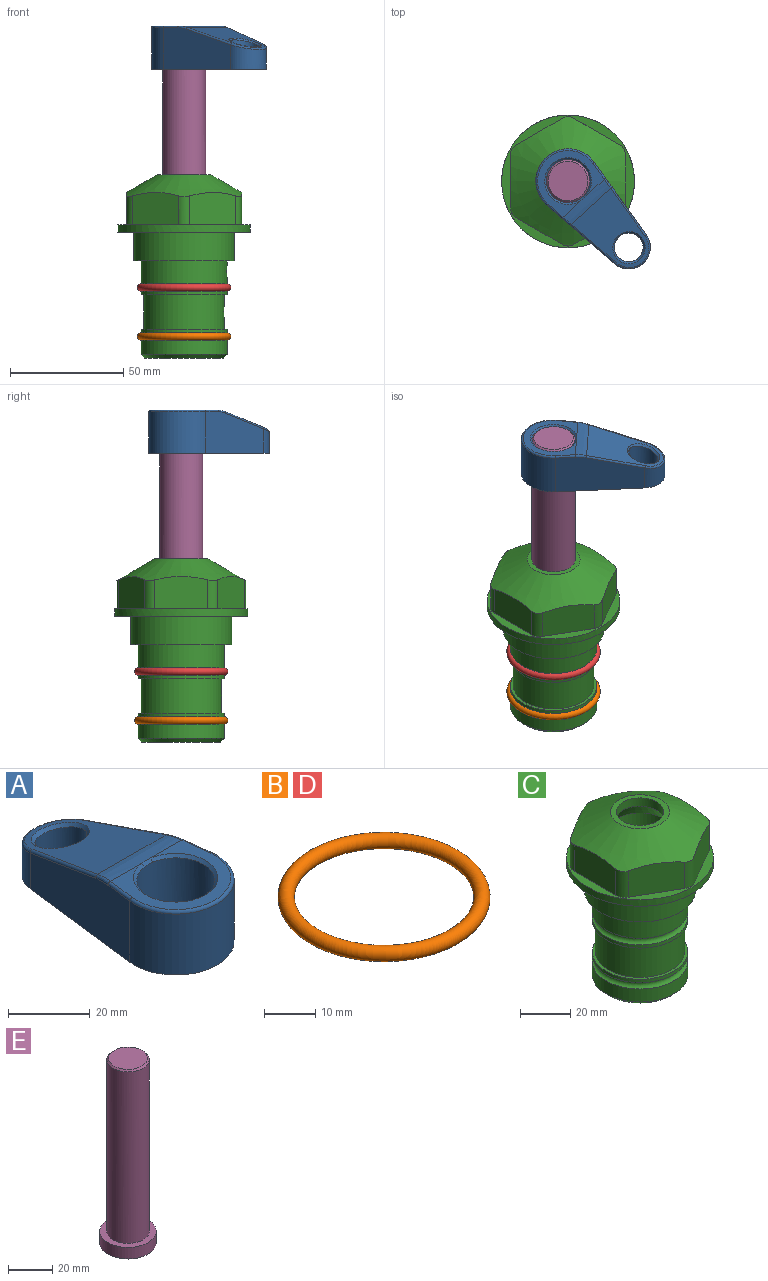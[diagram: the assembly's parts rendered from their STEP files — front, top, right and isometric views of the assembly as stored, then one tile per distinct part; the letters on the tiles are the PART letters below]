
ASSEMBLY  parts=5 mates=4
PART A: 31 faces, bbox 31.7x65.5x19.8 mm
  f0: plane 39.12x18.26mm, normal (0.99,0.12,0), area 612.2mm2, adj f1,f4,f7,f11,f13,f15
  f1: cylinder r=9.53mm len=18.91mm, axis (0,0,-1), area 296.1mm2, adj f0,f2,f7,f17
  f2: plane 39.12x18.26mm, normal (-0.99,0.12,0), area 612.2mm2, adj f1,f4,f7,f12,f14,f16
  f3: cylinder r=6.35mm len=12.7mm, axis (0,0,-1), area 362.4mm2, adj f7,f18
  f4: cylinder r=14.29mm len=28.58mm, axis (0,0,-1), area 882.2mm2, adj f0,f2,f7,f10
  f5: cylinder r=9.53mm len=19.05mm, axis (0,0,-1), area 1092.6mm2, adj f7,f19,f20
  f6: plane 26.99x23.69mm, normal (0,0,1), area 216.2mm2, adj f9,f10,f11,f12,f19
  f7: plane 63.5x28.58mm, normal (0,0,-1), area 661.8mm2, adj f0,f1,f2,f3,f4,f5,f22,f23
  f8: plane 33.52x23.6mm, normal (0,0.26,0.97), area 486mm2, adj f9,f15,f16,f17,f18
  f9: cylinder r=19.05mm len=24.72mm, axis (1,0,0), area 120.4mm2, adj f6,f8,f13,f14,f20
  f10: torus R=13.49mm, axis (0,0,1), area 59mm2, adj f4,f6,f11,f12
  f11: cylinder r=0.79mm len=8.67mm, axis (0.12,-0.99,0), area 10.8mm2, adj f0,f6,f10,f13
  f12: cylinder r=0.79mm len=8.67mm, axis (0.12,0.99,0), area 10.8mm2, adj f2,f6,f10,f14
  f13: bspline ~4.95x1.42mm, area 6.1mm2, adj f0,f9,f11,f15
  f14: bspline ~4.95x1.42mm, area 6.1mm2, adj f2,f9,f12,f16
  f15: cylinder r=0.79mm len=25.95mm, axis (0.12,-0.96,0.26), area 32.9mm2, adj f0,f8,f13,f17
  f16: cylinder r=0.79mm len=25.95mm, axis (0.12,0.96,-0.26), area 32.9mm2, adj f2,f8,f14,f17
  f17: bspline ~18.91x8.38mm, area 30mm2, adj f1,f8,f15,f16
  f18: bspline ~14.29x14.29mm, area 48.3mm2, adj f3,f8
  f19: cone r=9.53mm half-angle=45deg, axis (0,0,1), area 66.5mm2, adj f5,f6,f20
  f20: bspline ~3.22x0.96mm, area 3.5mm2, adj f5,f9,f19
  f21: plane 2.75x2.72mm, normal (0,0,-1), area 2.9mm2, adj f23,f25,f28
  f22: plane 23.05x15.88mm, normal (-0.99,-0.12,0), area 323.6mm2, adj f7,f25,f26,f27,f28,f29
  f23: plane 23.05x15.88mm, normal (0.99,-0.12,0), area 323.6mm2, adj f7,f21,f25,f27,f28,f30
  f24: cylinder r=9.53mm len=10.69mm, axis (0,0,-1), area 114.7mm2, adj f7,f27,f29,f30
  f25: cylinder r=12.7mm len=20.59mm, axis (0,0,-1), area 381.1mm2, adj f7,f21,f22,f23,f26,f28
  f26: plane 2.75x2.72mm, normal (0,0,-1), area 2.9mm2, adj f22,f25,f28
  f27: plane 19.72x18.37mm, normal (0,-0.26,-0.97), area 291.8mm2, adj f22,f23,f24,f28,f29,f30
  f28: cylinder r=15.88mm len=19.92mm, axis (1,0,0), area 54.8mm2, adj f21,f22,f23,f25,f26,f27
  f29: cylinder r=1.59mm len=11mm, axis (0,0,-1), area 34.7mm2, adj f7,f22,f24,f27
  f30: cylinder r=1.59mm len=11mm, axis (0,0,-1), area 34.7mm2, adj f7,f23,f24,f27
PART B: 1 faces, bbox 44.7x44.7x3.2 mm
  f0: torus R=19.05mm, axis (0,0,1), area 1193.9mm2
PART C: 36 faces, bbox 58.7x58.7x81 mm
  f0: cylinder r=17.78mm len=35.56mm, axis (0,0,1), area 1670.8mm2, adj f23,f24,f31
  f1: cylinder r=19.05mm len=38.1mm, axis (0,0,1), area 1191.9mm2, adj f26,f27,f30
  f2: plane 58.66x58.66mm, normal (0,0,-1), area 1150.6mm2, adj f3,f28
  f3: cylinder r=29.33mm len=58.66mm, axis (0,0,-1), area 585.1mm2, adj f2,f4
  f4: plane 58.66x58.66mm, normal (0,0,1), area 475.9mm2, adj f3,f5,f6,f7,f8,f9,f10,f11
  f5: plane 20.32x14.34mm, normal (-0.5,0.87,0), area 324.4mm2, adj f4,f15,f16,f17
  f6: plane 20.32x14.34mm, normal (0.5,0.87,0), area 324.4mm2, adj f4,f14,f15,f17
  f7: plane 23.48x14.34mm, normal (1,0,0), area 324.4mm2, adj f4,f13,f14,f17
  f8: plane 20.32x14.34mm, normal (0.5,-0.87,0), area 324.4mm2, adj f4,f12,f13,f17
  f9: plane 20.32x14.34mm, normal (-0.5,-0.87,0), area 324.4mm2, adj f4,f11,f12,f17
  f10: plane 23.48x14.34mm, normal (-1,0,0), area 324.4mm2, adj f4,f11,f16,f17
  f11: cylinder r=5.08mm len=12.85mm, axis (0,0,-1), area 67.2mm2, adj f4,f9,f10,f17
  f12: cylinder r=5.08mm len=12.85mm, axis (0,0,-1), area 67.2mm2, adj f4,f8,f9,f17
  f13: cylinder r=5.08mm len=12.85mm, axis (0,0,-1), area 67.2mm2, adj f4,f7,f8,f17
  f14: cylinder r=5.08mm len=12.85mm, axis (0,0,-1), area 67.2mm2, adj f4,f6,f7,f17
  f15: cylinder r=5.08mm len=12.85mm, axis (0,0,-1), area 67.2mm2, adj f4,f5,f6,f17
  f16: cylinder r=5.08mm len=12.85mm, axis (0,0,-1), area 67.2mm2, adj f4,f5,f10,f17
  f17: cone r=11.73mm half-angle=60deg, axis (0,0,-1), area 2071.8mm2, adj f5,f6,f7,f8,f9,f10,f11,f12
  f18: plane 23.46x23.46mm, normal (0,0,1), area 147.4mm2, adj f17,f35
  f19: plane 34.93x34.93mm, normal (0,0,-1), area 958mm2, adj f29
  f20: cylinder r=19.05mm len=38.1mm, axis (0,0,1), area 760.1mm2, adj f21,f29
  f21: torus R=19.05mm, axis (0,0,1), area 565.3mm2, adj f20,f22
  f22: cylinder r=19.05mm len=38.1mm, axis (0,0,1), area 190mm2, adj f21,f23
  f23: plane 38.1x38.1mm, normal (0,0,1), area 146.9mm2, adj f0,f22
  f24: plane 38.1x38.1mm, normal (0,0,-1), area 146.9mm2, adj f0,f25
  f25: cylinder r=19.05mm len=38.1mm, axis (0,0,1), area 190mm2, adj f24,f26
  f26: torus R=19.05mm, axis (0,0,1), area 565.3mm2, adj f1,f25
  f27: plane 44.45x44.45mm, normal (0,0,-1), area 411.7mm2, adj f1,f28
  f28: cylinder r=22.23mm len=44.45mm, axis (0,0,1), area 1773.5mm2, adj f2,f27
  f29: cone r=19.05mm half-angle=45deg, axis (0,0,1), area 257.5mm2, adj f19,f20
  f30: cylinder r=3.17mm len=6.75mm, axis (-1,0,0), area 128mm2, adj f1,f33
  f31: cylinder r=3.17mm len=6.35mm, axis (-1,0,0), area 102.5mm2, adj f0,f33
  f32: plane 25.4x25.4mm, normal (0,0,1), area 506.7mm2, adj f33
  f33: cylinder r=12.7mm len=66.42mm, axis (0,0,-1), area 5236.2mm2, adj f30,f31,f32,f34
  f34: cone r=9.53mm half-angle=30deg, axis (0,0,-1), area 443.4mm2, adj f33,f35
  f35: cylinder r=9.53mm len=19.05mm, axis (0,0,-1), area 240.9mm2, adj f18,f34
PART D: same geometry as B
PART E: 6 faces, bbox 25.4x25.4x101.6 mm
  f0: plane 17.46x17.46mm, normal (0,0,1), area 239.5mm2, adj f5
  f1: plane 25.4x25.4mm, normal (0,0,-1), area 506.7mm2, adj f2
  f2: cylinder r=12.7mm len=25.4mm, axis (0,0,1), area 506.7mm2, adj f1,f3
  f3: plane 25.4x25.4mm, normal (0,0,1), area 221.7mm2, adj f2,f4
  f4: cylinder r=9.53mm len=94.46mm, axis (0,0,1), area 5653mm2, adj f3,f5
  f5: cone r=8.73mm half-angle=45deg, axis (0,0,-1), area 64.4mm2, adj f0,f4
PLACE A rot(axis=(0,0,-1),137.5deg) t=(0,0,27.55)mm
PLACE B t=(0,0,-21.59)mm
PLACE C at identity fixed
PLACE D at identity
PLACE E rot(axis=(0,0,-1),137.5deg) t=(0,0,27.55)mm
MATE fastened D.f0 <-> C.f0  axis (0,0,1) through (0,0,-24.51)mm
MATE fastened B.f0 <-> C.f0  axis (0,0,1) through (0,0,-46.1)mm
MATE fastened E.f2 <-> A.f4  axis (0,0,1) through (0,0,91.05)mm
MATE cylindrical C.f0 <-> E.f2  axis (0,0,1) through (0,0,-50.55)mm
